# Revit family: Faucet-Lavatory-American_Standard-Monterrey-6540.27x_Series
name_source: partatom
category: Plumbing Fixtures
units: mm (PartAtom-declared; Revit-internal decimal feet)

## family parameters
Always vertical = No
Cut with Voids When Loaded = No
OmniClass Number = 23.45.55.17
OmniClass Title = Mixing Faucets
Part Type = Normal
Room Calculation Point = No
Round Connector Dimension = Use Diameter
Shared = Yes
Work Plane-Based = Yes

## types (2) — shared parameters
ADA Compliant = Yes
Assembly Code = D2020300
CW Connection = Yes
CWFU = 1.5
Cold Water Connection Diameter = 1/2"
Default Elevation = 0"
Description = Monterrey Two-Handle 8" Widespread Lavatory Faucet with Rigid/Swivel Goosneck Spout with 5" Reach and Flexible Underbody.
Finish = Metal-American Standard-002-Polished Chrome
HW Connection = Yes
HWFU = 1.5
Height = 10 5/8"
Hot Water Connection Diameter = 1/2"
IAPMO Compliance = These products meet or exceeds: ASME A112.18.1,CSA B125.1,NSF 372
Installation Type = Deck Mounted
Length = 15 3/4"
Manufacturer = American Standard
Material = Metal-American Standard-002-Polished Chrome
Price = Prices may vary. Please consult Manufacturer Representative for most up-to-date price list.
Product Documentation Link = https://www.americanstandard-us.com
Product Page URL = https://www.americanstandard-us.com
Revised Date = 06/08/2021
URL = http://www.americanstandard-us.com
Vent Connection = No
Waste Connection = No
Width = 5"
zero-valued in all types: WFU

## per-type parameters (varying)
| type | Flow Rate |
| 6540.270.002 | 1.5 gpm (5.7 L/min) |
| 6540.275.002 | 0.5 gpm (1.9 L/min) |

note: column(s) folded — value = type name in every type: Model

## geometry (parser evidence)
native form markers: Sweep x2
no freeform markers — native parametric forms only
